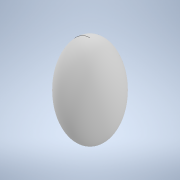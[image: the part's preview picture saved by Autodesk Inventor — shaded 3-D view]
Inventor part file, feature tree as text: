
AUTODESK INVENTOR PART (.ipt)
format: ipt  version: 2022 (Build 260153000, 153)  size: 211,968 bytes
history: native  units: in
note: dims shown in document units (in); Inventor stores cm internally (conversion verified against a paired STEP export)
features: revolve x1, sketch x1
ambient origin geometry x8: Origin, YZ Plane, XZ Plane, XY Plane, X Axis, Y Axis, Z Axis, Center Point
bodies: Solid1 (feature_tree)
feature tree (2):
  revolve  "Revolution1"  [1 undecoded]
  sketch  "Sketch1"  dims[d0=90.0deg]
note: 1 required parameter value undecoded (feature->parameter linkage not recoverable at this tier; creation-order binding heuristic only, values carry confidence <= 0.55)
